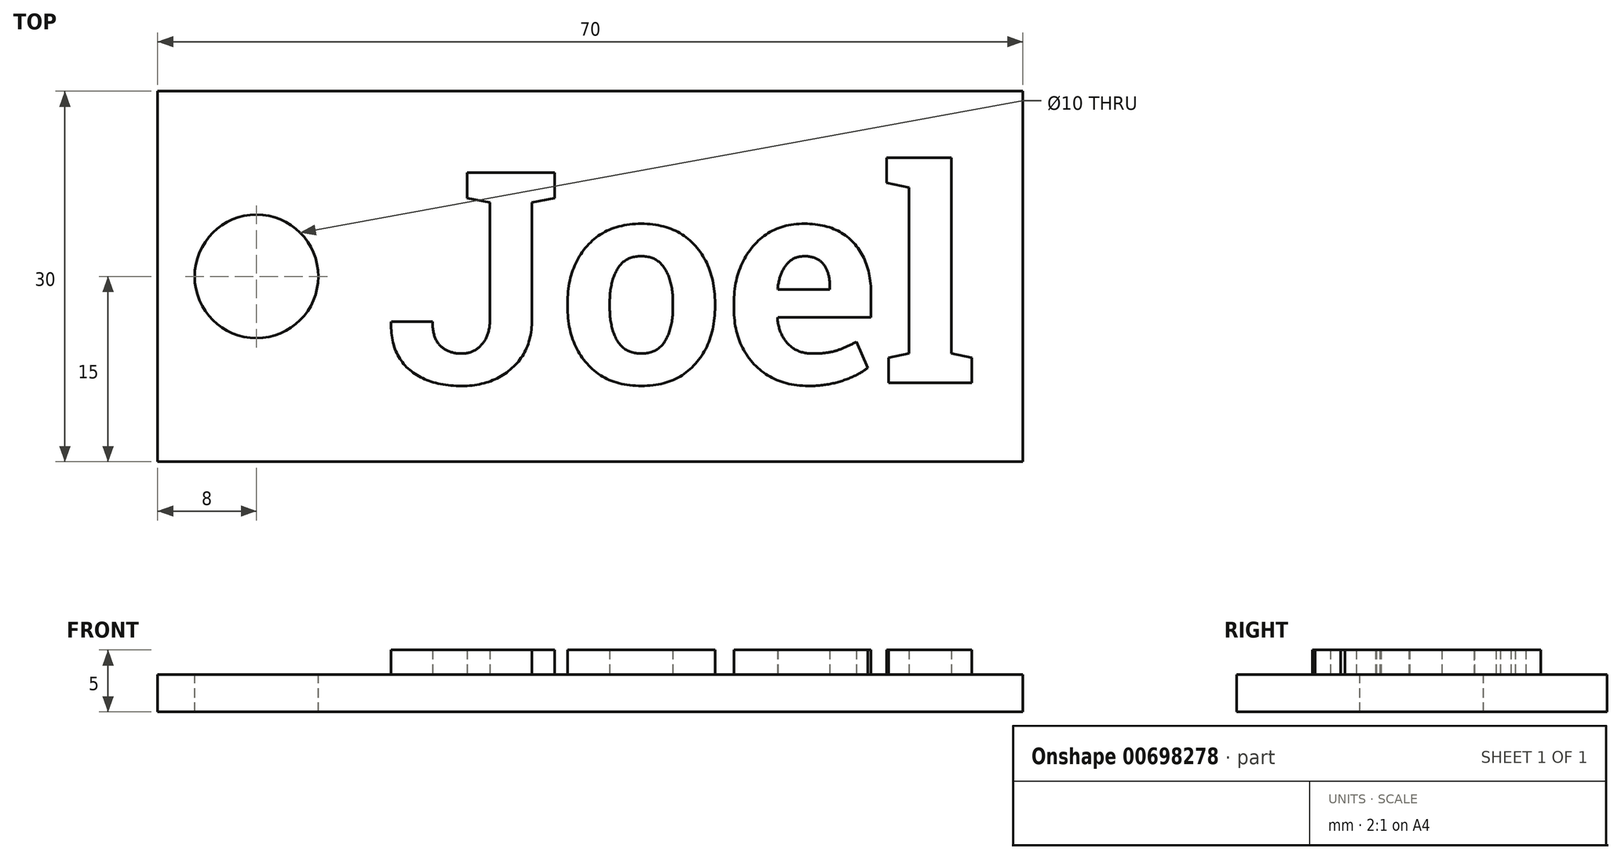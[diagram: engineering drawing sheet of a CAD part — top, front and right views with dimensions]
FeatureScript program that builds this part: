
annotation { "Feature Type Name" : "Feature", "Feature Type Description" : "" }
export const myFeature = defineFeature(function(context is Context, id is Id, definition is map)
    precondition{}
    {
        {
            var Q0;
            Q0=qCreatedBy(makeId("Top.planeOp"),FACE);
            var sketch = newSketch(context, id + "F0", { "sketchPlane" : qUnion([Q0])});
            skLineSegment(sketch, "E0.bottom", {"start": v(-35, 15) * mm, "end": v(35, 15) * mm});
            skLineSegment(sketch, "E0.top", {"start": v(-35, -15) * mm, "end": v(35, -15) * mm});
            skLineSegment(sketch, "E0.left", {"start": v(-35, 15) * mm, "end": v(-35, -15) * mm});
            skLineSegment(sketch, "E0.right", {"start": v(35, 15) * mm, "end": v(35, -15) * mm});
            skSolve(sketch);
        }
        {
            var Q0;
            Q0 = qSketchRegion(id + "F0", true);
            extrude(context, id + "F1", {"entities" : qUnion([Q0]), "depth" : 3 * mm, "offsetDistance" : 25 * mm});
        }
        {
            var Q0;
            Q0=makeQuery(id+"F1.opExtrude","CAP_FACE",FACE,{"disambiguationData":[OSD([sQuery(id+"F0.wireOp",EDGE,"E0.bottom"),sQuery(id+"F0.wireOp",EDGE,"E0.top"),sQuery(id+"F0.wireOp",EDGE,"E0.left"),sQuery(id+"F0.wireOp",EDGE,"E0.right")])],"isStart":false});
            var sketch = newSketch(context, id + "F2", { "sketchPlane" : qUnion([Q0])});
            skText(sketch, "E1", { "text": "Joel", "fontName": "RobotoSlab-Bold.ttf"});
            const initialGuessF2  = {"E1": [-0.01651, -0.00862, 1, 0, 0.01724]};
            skSetInitialGuess(sketch, initialGuessF2);
            skSolve(sketch);
        }
        {
            var Q0;
            Q0 = qSketchRegion(id + "F2", true);
            extrude(context, id + "F3", {"entities" : qUnion([Q0]), "operationType" : NewBodyOperationType.ADD, "depth" : 2 * mm, "offsetDistance" : 25 * mm});
        }
        {
            var Q0;
            {var subQ0=sQuery(id+"F0.wireOp",EDGE,"E0.left");var subQ1=sQuery(id+"F0.wireOp",EDGE,"E0.bottom");var subQ2=sQuery(id+"F0.wireOp",EDGE,"E0.right");var subQ3=sQuery(id+"F0.wireOp",EDGE,"E0.top");Q0=makeQuery(id+"F3.boolean.opBoolean","SPLIT",FACE,{"disambiguationData":[TD([makeQuery(id+"F1.opExtrude","SWEPT_FACE",FACE,{"disambiguationData":[OSD([subQ1])]})])],"derivedFrom":makeQuery(id+"F1.opExtrude","CAP_FACE",FACE,{"disambiguationData":[OSD([subQ1,subQ3,subQ0,subQ2])],"isStart":false})});}
            var sketch = newSketch(context, id + "F4", { "sketchPlane" : qUnion([Q0])});
            skCircle(sketch, "E2", {"center": v(-27, 0) * mm, "radius": 5 * mm});
            skSolve(sketch);
        }
        {
            var Q0;
            Q0 = qSketchRegion(id + "F4", true);
            extrude(context, id + "F5", {"entities" : qUnion([Q0]), "operationType" : NewBodyOperationType.REMOVE, "endBound" : BoundingType.THROUGH_ALL, "oppositeDirection" : true, "depth" : 25 * mm, "offsetDistance" : 25 * mm});
        }
    });
